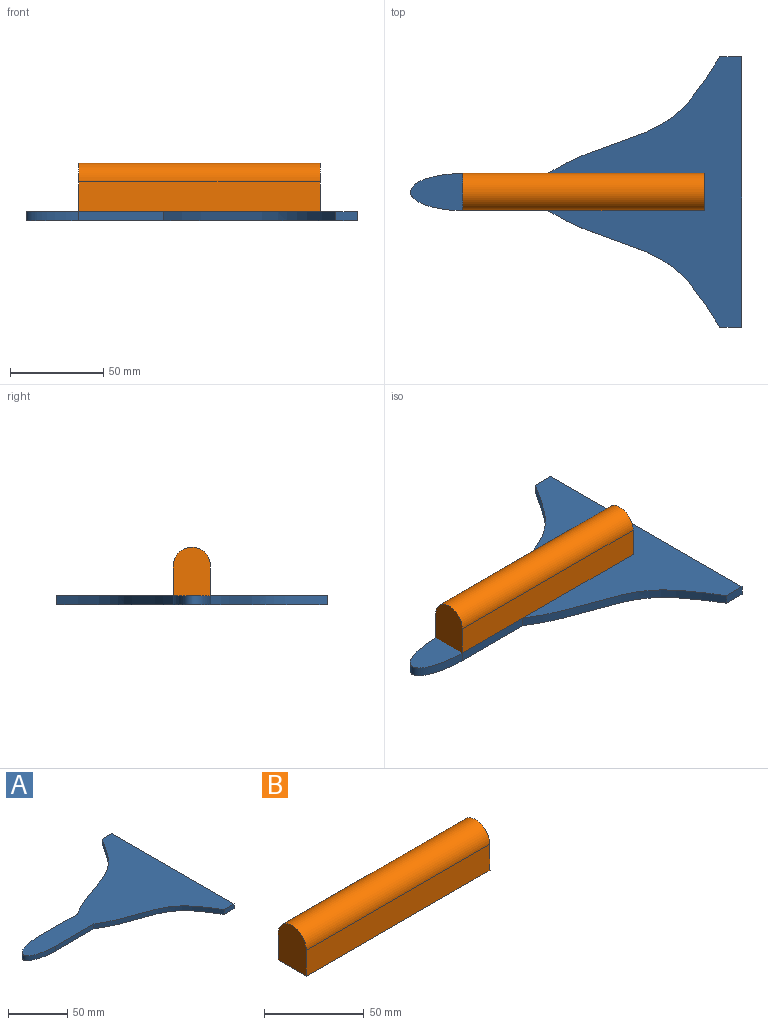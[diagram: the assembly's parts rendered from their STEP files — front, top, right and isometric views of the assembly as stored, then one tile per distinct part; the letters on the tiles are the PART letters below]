
ASSEMBLY  parts=2 mates=1
PART A: 10 faces, bbox 178x145.3x5 mm
  f0: extruded ~92.34x62.67mm, area 575.7mm2, adj f1,f7,f8,f9
  f1: plane 11.76x5mm, normal (0,-1,0), area 58.8mm2, adj f0,f2,f8,f9
  f2: plane 145.34x5mm, normal (1,0,0), area 726.7mm2, adj f1,f3,f8,f9
  f3: plane 11.76x5mm, normal (0,1,0), area 58.8mm2, adj f2,f4,f8,f9
  f4: extruded ~92.34x62.67mm, area 575.7mm2, adj f3,f5,f8,f9
  f5: plane 45.9x5mm, normal (0,1,0), area 229.5mm2, adj f4,f6,f8,f9
  f6: extruded ~28x20mm, area 315.4mm2, adj f5,f7,f8,f9
  f7: plane 45.9x5mm, normal (0,-1,0), area 229.5mm2, adj f0,f6,f8,f9
  f8: plane 178x145.34mm, normal (0,0,1), area 9182.3mm2, adj f0,f1,f2,f3,f4,f5,f6,f7
  f9: plane 178x145.34mm, normal (0,0,-1), area 9182.3mm2, adj f0,f1,f2,f3,f4,f5,f6,f7
PART B: 6 faces, bbox 130x20.1x26 mm
  f0: plane 130x15.89mm, normal (0,1,-0.01), area 2066mm2, adj f1,f3,f4,f5
  f1: cylinder r=10mm len=130mm, axis (-1,0,0), area 4111.6mm2, adj f0,f2,f4,f5
  f2: plane 130x15.9mm, normal (0,-1,0.01), area 2066.6mm2, adj f1,f3,f4,f5
  f3: plane 130x20mm, normal (0,0,-1), area 2600mm2, adj f0,f2,f4,f5
  f4: plane 26x20.09mm, normal (1,0,0), area 477.1mm2, adj f0,f1,f2,f3
  f5: plane 26x20.09mm, normal (-1,0,0), area 477.1mm2, adj f0,f1,f2,f3
PLACE A t=(-68.69,11.04,-43.44)mm
PLACE B t=(-177.8,11.12,-50.11)mm
MATE fastened B.f3 <-> A.f8  axis (0,0,-1) through (-177.8,11.04,-38.44)mm
